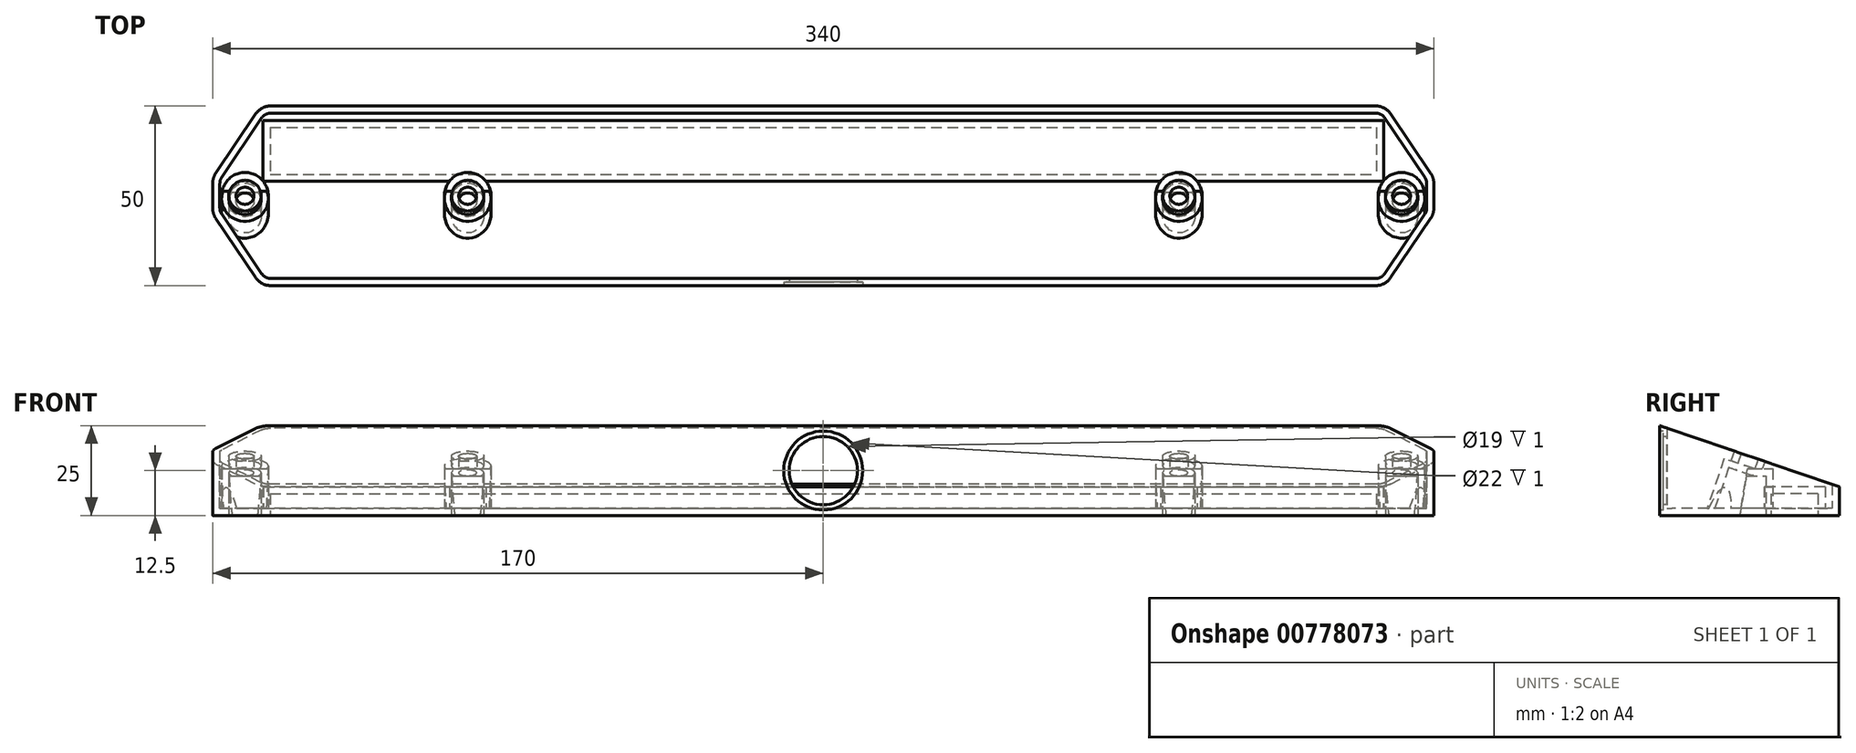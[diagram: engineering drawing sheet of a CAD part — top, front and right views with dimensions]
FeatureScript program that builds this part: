
annotation { "Feature Type Name" : "Feature", "Feature Type Description" : "" }
export const myFeature = defineFeature(function(context is Context, id is Id, definition is map)
    precondition{}
    {
        {
            var Q0;
            Q0=qCreatedBy(makeId("Right.planeOp"),FACE);
            var sketch = newSketch(context, id + "F0", { "sketchPlane" : qUnion([Q0])});
            skLineSegment(sketch, "E0", {"start": v(0, 0) * mm, "end": v(0, 25) * mm});
            skLineSegment(sketch, "E1", {"start": v(0, 25) * mm, "end": v(50, 8) * mm});
            skLineSegment(sketch, "E2", {"start": v(50, 8) * mm, "end": v(50, 0) * mm});
            skLineSegment(sketch, "E3", {"start": v(50, 0) * mm, "end": v(0, 0) * mm});
            skSolve(sketch);
        }
        {
            var Q0;
            Q0=makeQuery(id+"F0.imprint","IMPRINT",FACE,{"disambiguationData":[TD([[makeQuery(id+"F0.imprint","IMPRINT",EDGE,{"derivedFrom":sQuery(id+"F0.wireOp",EDGE,"E0")}),-1.0]])]});
            extrude(context, id + "F1", {"entities" : qUnion([Q0]), "depth" : 340 * mm, "offsetDistance" : 25.4 * mm});
        }
        {
            var Q0;
            Q0=makeQuery(id+"F1.opExtrude","SWEPT_FACE",FACE,{"disambiguationData":[OSD([sQuery(id+"F0.wireOp",EDGE,"E3")])]});
            var sketch = newSketch(context, id + "F2", { "sketchPlane" : qUnion([Q0])});
            skLineSegment(sketch, "E4", {"start": v(0, -25) * mm, "end": v(340, -25) * mm, "construction": true});
            skLineSegment(sketch, "E5.0", {"start": v(0, -30) * mm, "end": v(340, -30) * mm, "construction": true});
            skLineSegment(sketch, "E6.0", {"start": v(0, -20) * mm, "end": v(340, -20) * mm, "construction": true});
            skLineSegment(sketch, "E7", {"start": v(13.5, 24.96) * mm, "end": v(13.5, -64.67) * mm, "construction": true});
            skLineSegment(sketch, "E8", {"start": v(326.5, 17.13) * mm, "end": v(326.5, -69.89) * mm, "construction": true});
            skLineSegment(sketch, "E9", {"start": v(0.86, -18.73) * mm, "end": v(12.01, -2.2) * mm});
            skLineSegment(sketch, "E10", {"start": v(16.16, 0) * mm, "end": v(323.84, 0) * mm});
            skLineSegment(sketch, "E11", {"start": v(327.99, -2.2) * mm, "end": v(339.14, -18.73) * mm});
            skLineSegment(sketch, "E12", {"start": v(339.14, -31.27) * mm, "end": v(327.99, -47.8) * mm});
            skLineSegment(sketch, "E13", {"start": v(323.84, -50) * mm, "end": v(16.16, -50) * mm});
            skLineSegment(sketch, "E14", {"start": v(12.01, -47.8) * mm, "end": v(0.86, -31.27) * mm});
            skPoint(sketch, "E15.visualSharp", {"position": v(13.5, 0) * mm});
            skArc(sketch, "E15.filletArc", {"start": v(16.16, 0) * mm, "mid": v(13.81, -0.58) * mm, "end": v(12.01, -2.2) * mm});
            skPoint(sketch, "E16.visualSharp", {"position": v(13.5, -50) * mm});
            skArc(sketch, "E16.filletArc", {"start": v(12.01, -47.8) * mm, "mid": v(13.81, -49.42) * mm, "end": v(16.16, -50) * mm});
            skPoint(sketch, "E17.visualSharp", {"position": v(326.5, 0) * mm});
            skArc(sketch, "E17.filletArc", {"start": v(327.99, -2.2) * mm, "mid": v(326.19, -0.58) * mm, "end": v(323.84, 0) * mm});
            skPoint(sketch, "E18.visualSharp", {"position": v(326.5, -50) * mm});
            skArc(sketch, "E18.filletArc", {"start": v(323.84, -50) * mm, "mid": v(326.19, -49.42) * mm, "end": v(327.99, -47.8) * mm});
            skLineSegment(sketch, "E19", {"start": v(340, -21.53) * mm, "end": v(340, -28.47) * mm});
            skPoint(sketch, "E20.visualSharp", {"position": v(340, -20) * mm});
            skArc(sketch, "E20.filletArc", {"start": v(340, -21.53) * mm, "mid": v(339.78, -20.07) * mm, "end": v(339.14, -18.73) * mm});
            skPoint(sketch, "E21.visualSharp", {"position": v(340, -30) * mm});
            skArc(sketch, "E21.filletArc", {"start": v(339.14, -31.27) * mm, "mid": v(339.78, -29.93) * mm, "end": v(340, -28.47) * mm});
            skLineSegment(sketch, "E22", {"start": v(0, -21.53) * mm, "end": v(0, -28.47) * mm});
            skPoint(sketch, "E23.visualSharp", {"position": v(0, -20) * mm});
            skArc(sketch, "E23.filletArc", {"start": v(0.86, -18.73) * mm, "mid": v(0.22, -20.07) * mm, "end": v(0, -21.53) * mm});
            skPoint(sketch, "E24.visualSharp", {"position": v(0, -30) * mm});
            skArc(sketch, "E24.filletArc", {"start": v(0, -28.47) * mm, "mid": v(0.22, -29.93) * mm, "end": v(0.86, -31.27) * mm});
            skSolve(sketch);
        }
        {
            var Q0;
            Q0=makeQuery(id+"F2.imprint","IMPRINT",FACE,{"disambiguationData":[TD([[makeQuery(id+"F2.imprint","IMPRINT",EDGE,{"derivedFrom":sQuery(id+"F2.wireOp",EDGE,"E9")}),1.0]])]});
            var Q1;
            Q1=makeQuery(id+"F2.imprint","IMPRINT",FACE,{"disambiguationData":[TD([[makeQuery(id+"F2.imprint","IMPRINT",EDGE,{"derivedFrom":sQuery(id+"F2.wireOp",EDGE,"E14")}),1.0]])]});
            var Q2;
            Q2=makeQuery(id+"F2.imprint","IMPRINT",FACE,{"disambiguationData":[TD([[makeQuery(id+"F2.imprint","IMPRINT",EDGE,{"derivedFrom":sQuery(id+"F2.wireOp",EDGE,"E12")}),1.0]])]});
            var Q3;
            Q3=makeQuery(id+"F2.imprint","IMPRINT",FACE,{"disambiguationData":[TD([[makeQuery(id+"F2.imprint","IMPRINT",EDGE,{"derivedFrom":sQuery(id+"F2.wireOp",EDGE,"E11")}),1.0]])]});
            extrude(context, id + "F3", {"entities" : qUnion([Q0, Q1, Q2, Q3]), "operationType" : NewBodyOperationType.REMOVE, "oppositeDirection" : true, "depth" : 25 * mm, "offsetDistance" : 25 * mm});
        }
        {
            var Q0;
            Q0=makeQuery(id+"F1.opExtrude","SWEPT_FACE",FACE,{"disambiguationData":[OSD([sQuery(id+"F0.wireOp",EDGE,"E1")])]});
            var Q1;
            Q1 = qBodyType(qCreatedBy(id + "F5" ,EDGE), BodyType.WIRE);
            cPlane(context, id + "F4", {"entities" : qUnion([Q0, Q1]), "cplaneType" : CPlaneType.OFFSET, "offset" : 20 * mm, "oppositeDirection" : true, "width" : 150 * mm, "height" : 150 * mm});
        }
        {
            var Q0;
            Q0=qCreatedBy(id+"F4.planeOp",FACE);
            var sketch = newSketch(context, id + "F5", { "sketchPlane" : qUnion([Q0])});
            skLineSegment(sketch, "E25", {"start": v(340, 18.36) * mm, "end": v(211.64, 18.36) * mm, "construction": true});
            skLineSegment(sketch, "E26", {"start": v(331, 56.87) * mm, "end": v(331, -14.6) * mm, "construction": true});
            skPoint(sketch, "E27", {"position": v(331, 18.36) * mm});
            skLineSegment(sketch, "E28", {"start": v(0, 18.36) * mm, "end": v(122.54, 18.36) * mm, "construction": true});
            skLineSegment(sketch, "E29", {"start": v(9, 57.76) * mm, "end": v(9, -13.12) * mm, "construction": true});
            skPoint(sketch, "E30", {"position": v(9, 18.36) * mm});
            skLineSegment(sketch, "E31.0", {"start": v(71, 57.76) * mm, "end": v(71, -13.12) * mm, "construction": true});
            skLineSegment(sketch, "E32.0", {"start": v(269, 56.87) * mm, "end": v(269, -14.6) * mm, "construction": true});
            skPoint(sketch, "E33", {"position": v(71, 18.36) * mm});
            skPoint(sketch, "E34", {"position": v(269, 18.36) * mm});
            skSolve(sketch);
        }
        {
            var Q0;
            Q0=sQuery(id+"F5.wireOp",VERTEX,"E30");
            var Q1;
            Q1=sQuery(id+"F5.wireOp",VERTEX,"E27");
            var Q2;
            Q2=sQuery(id+"F5.wireOp",VERTEX,"E33");
            var Q3;
            Q3=sQuery(id+"F5.wireOp",VERTEX,"E34");
            var Q4;
            Q4=makeQuery(id+"F1.opExtrude","SWEPT_BODY",BODY,{"disambiguationData":[OSD([sQuery(id+"F0.wireOp",EDGE,"E0"),sQuery(id+"F0.wireOp",EDGE,"E1"),sQuery(id+"F0.wireOp",EDGE,"E2"),sQuery(id+"F0.wireOp",EDGE,"E3")])]});
            hole(context, id + "F6", {"style" : HoleStyle.C_BORE, "endStyle" : HoleEndStyle.THROUGH, "oppositeDirection" : true, "holeDiameter" : 5 * mm, "cBoreDiameter" : 9 * mm, "cBoreDepth" : 11 * mm, "majorDiameter" : 5 * mm, "isTappedThrough" : true, "tappedDepth" : 12 * mm, "tapClearance" : 3, "locations" : qUnion([Q0, Q1, Q2, Q3]), "scope" : qUnion([Q4])});
        }
        {
            var Q0;
            Q0=makeQuery(id+"F1.opExtrude","SWEPT_FACE",FACE,{"disambiguationData":[OSD([sQuery(id+"F0.wireOp",EDGE,"E3")])]});
            var sketch = newSketch(context, id + "F7", { "sketchPlane" : qUnion([Q0])});
            skLineSegment(sketch, "E35", {"start": v(0, -25) * mm, "end": v(81.27, -25) * mm, "construction": true});
            skLineSegment(sketch, "E36", {"start": v(9, -36.78) * mm, "end": v(9, -3.11) * mm, "construction": true});
            skPoint(sketch, "E36.endSnap0", {"position": v(9, -14.64) * mm});
            skPoint(sketch, "E37", {"position": v(9, -25) * mm});
            skLineSegment(sketch, "E38", {"start": v(340, -25) * mm, "end": v(255.6, -25) * mm, "construction": true});
            skLineSegment(sketch, "E39", {"start": v(331, -6.96) * mm, "end": v(331, -42.16) * mm, "construction": true});
            skPoint(sketch, "E40", {"position": v(331, -25) * mm});
            skLineSegment(sketch, "E41", {"start": v(269, -6.83) * mm, "end": v(269, -36.64) * mm, "construction": true});
            skPoint(sketch, "E42", {"position": v(269, -25) * mm});
            skLineSegment(sketch, "E43", {"start": v(71, -3.82) * mm, "end": v(71, -34.89) * mm, "construction": true});
            skPoint(sketch, "E44", {"position": v(71, -25) * mm});
            skLineSegment(sketch, "E45", {"start": v(16, 12.73) * mm, "end": v(16, -57.61) * mm, "construction": true});
            skLineSegment(sketch, "E46", {"start": v(81.89, -31) * mm, "end": v(11, -31) * mm, "construction": true});
            skLineSegment(sketch, "E47", {"start": v(13.5, -44) * mm, "end": v(81.47, -44) * mm, "construction": true});
            skPoint(sketch, "E47.startSnap0", {"position": v(13.5, -19.4) * mm});
            skLineSegment(sketch, "E48", {"start": v(81.89, -31) * mm, "end": v(361.04, -31) * mm, "construction": true});
            skLineSegment(sketch, "E49", {"start": v(81.47, -44) * mm, "end": v(361.04, -44) * mm, "construction": true});
            skLineSegment(sketch, "E50", {"start": v(324, -58.77) * mm, "end": v(324, -17.97) * mm, "construction": true});
            skPoint(sketch, "E51", {"position": v(324, -31) * mm});
            skPoint(sketch, "E52", {"position": v(324, -44) * mm});
            skPoint(sketch, "E53", {"position": v(16, -31) * mm});
            skPoint(sketch, "E54", {"position": v(16, -44) * mm});
            skLineSegment(sketch, "E55.bottom", {"start": v(16, -44) * mm, "end": v(324, -44) * mm});
            skLineSegment(sketch, "E55.top", {"start": v(16, -31) * mm, "end": v(324, -31) * mm});
            skLineSegment(sketch, "E55.left", {"start": v(16, -44) * mm, "end": v(16, -31) * mm});
            skLineSegment(sketch, "E55.right", {"start": v(324, -44) * mm, "end": v(324, -31) * mm});
            skSolve(sketch);
        }
        {
            var Q0;
            Q0=sQuery(id+"F7.wireOp",VERTEX,"E37");
            var Q1;
            Q1=sQuery(id+"F7.wireOp",VERTEX,"E40");
            var Q2;
            Q2=sQuery(id+"F7.wireOp",VERTEX,"E44");
            var Q3;
            Q3=sQuery(id+"F7.wireOp",VERTEX,"E42");
            var Q4;
            Q4=makeQuery(id+"F1.opExtrude","SWEPT_BODY",BODY,{"disambiguationData":[OSD([sQuery(id+"F0.wireOp",EDGE,"E0"),sQuery(id+"F0.wireOp",EDGE,"E1"),sQuery(id+"F0.wireOp",EDGE,"E2"),sQuery(id+"F0.wireOp",EDGE,"E3")])]});
            hole(context, id + "F8", {"style" : HoleStyle.C_BORE, "endStyle" : HoleEndStyle.THROUGH, "holeDiameter" : .1 * mm, "cBoreDiameter" : 9 * mm, "cBoreDepth" : 11 * mm, "majorDiameter" : 5 * mm, "isTappedThrough" : true, "tappedDepth" : 12 * mm, "tapClearance" : 3, "startFromSketch" : true, "locations" : qUnion([Q0, Q1, Q2, Q3]), "scope" : qUnion([Q4])});
        }
        {
            var Q0;
            Q0 = qSketchRegion(id + "F7", true);
            extrude(context, id + "F9", {"entities" : qUnion([Q0]), "operationType" : NewBodyOperationType.REMOVE, "oppositeDirection" : true, "depth" : 6 * mm, "offsetDistance" : 25 * mm});
        }
        {
            var Q0;
            Q0=makeQuery(id+"F1.opExtrude","SWEPT_FACE",FACE,{"disambiguationData":[OSD([sQuery(id+"F0.wireOp",EDGE,"E1")])]});
            shell(context, id + "F10", {"entities" : qUnion([Q0]), "thickness" : 2 * mm});
        }
        {
            var Q0;
            Q0=makeQuery(id+"F1.opExtrude","SWEPT_FACE",FACE,{"disambiguationData":[OSD([sQuery(id+"F0.wireOp",EDGE,"E0")])]});
            var sketch = newSketch(context, id + "F11", { "sketchPlane" : qUnion([Q0])});
            skLineSegment(sketch, "E56", {"start": v(16.16, 12.5) * mm, "end": v(323.84, 12.5) * mm, "construction": true});
            skLineSegment(sketch, "E57", {"start": v(170, 25) * mm, "end": v(170, -5.98) * mm, "construction": true});
            skPoint(sketch, "E58", {"position": v(170, 12.5) * mm});
            skSolve(sketch);
        }
        {
            var Q0;
            Q0=sQuery(id+"F11.wireOp",VERTEX,"E58");
            var Q1;
            Q1=makeQuery(id+"F1.opExtrude","SWEPT_BODY",BODY,{"disambiguationData":[OSD([sQuery(id+"F0.wireOp",EDGE,"E0"),sQuery(id+"F0.wireOp",EDGE,"E1"),sQuery(id+"F0.wireOp",EDGE,"E2"),sQuery(id+"F0.wireOp",EDGE,"E3")])]});
            hole(context, id + "F12", {"style" : HoleStyle.C_BORE, "endStyle" : HoleEndStyle.BLIND, "holeDiameter" : 19 * mm, "cBoreDiameter" : 22 * mm, "cBoreDepth" : 1 * mm, "majorDiameter" : 5 * mm, "holeDepth" : 12 * mm, "isTappedThrough" : true, "tappedDepth" : 12 * mm, "tapClearance" : 3, "startFromSketch" : true, "locations" : qUnion([Q0]), "scope" : qUnion([Q1])});
        }
    });
